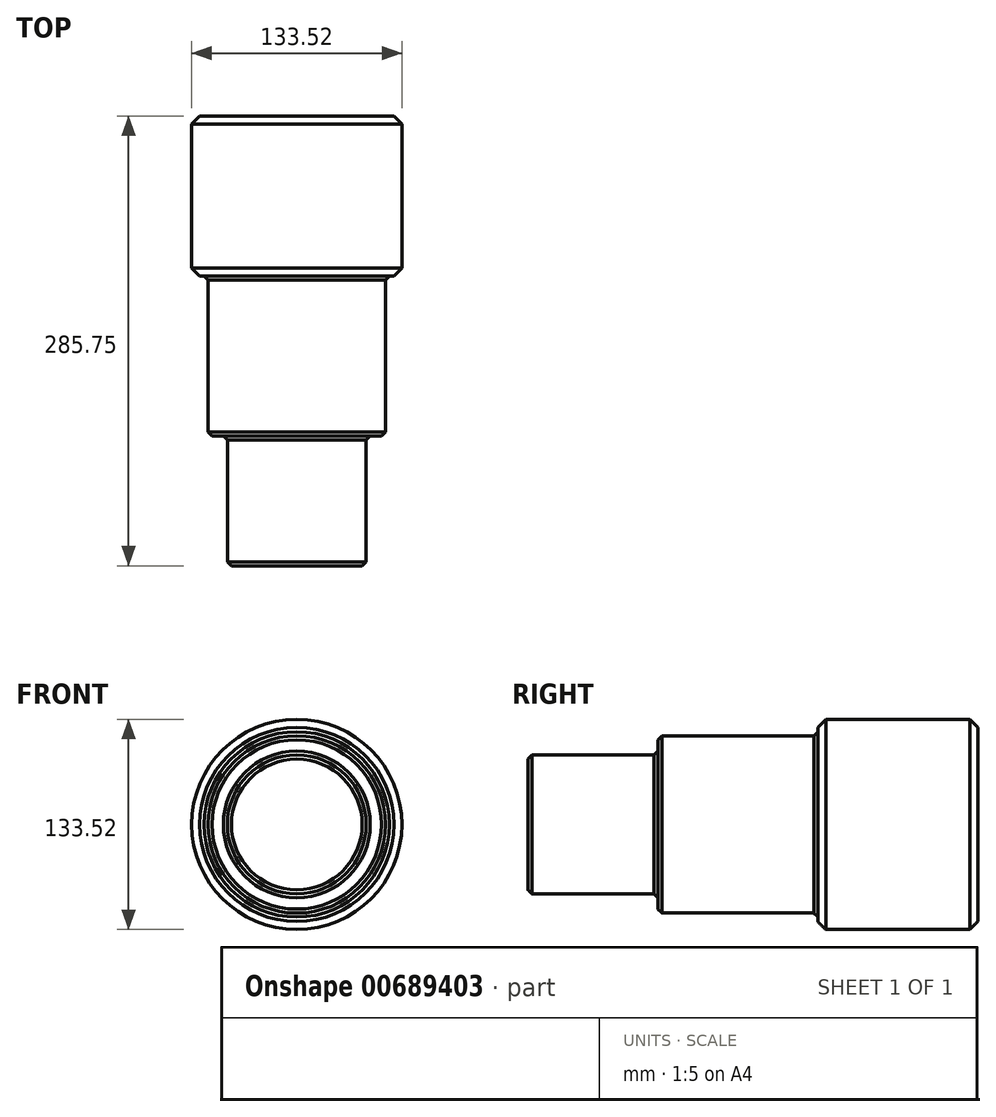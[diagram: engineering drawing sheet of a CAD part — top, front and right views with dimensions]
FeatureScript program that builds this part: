
annotation { "Feature Type Name" : "Feature", "Feature Type Description" : "" }
export const myFeature = defineFeature(function(context is Context, id is Id, definition is map)
    precondition{}
    {
        {
            var Q0;
            Q0=qCreatedBy(makeId("Front.planeOp"),FACE);
            var sketch = newSketch(context, id + "F0", { "sketchPlane" : qUnion([Q0])});
            skCircle(sketch, "E0", {"center": v(0, 0) * mm, "radius": 66.76 * mm});
            skSolve(sketch);
        }
        {
            var Q0;
            Q0 = qSketchRegion(id + "F0", true);
            extrude(context, id + "F1", {"entities" : qUnion([Q0]), "depth" : 101.6 * mm, "offsetDistance" : 25.4 * mm});
        }
        {
            var Q0;
            Q0=makeQuery(id+"F1.opExtrude","CAP_FACE",FACE,{"disambiguationData":[OSD([sQuery(id+"F0.wireOp",EDGE,"E0")])],"isStart":false});
            var sketch = newSketch(context, id + "F2", { "sketchPlane" : qUnion([Q0])});
            skCircle(sketch, "E1", {"center": v(0, 0) * mm, "radius": 56.32 * mm});
            skSolve(sketch);
        }
        {
            var Q0;
            Q0 = qSketchRegion(id + "F2", true);
            extrude(context, id + "F3", {"entities" : qUnion([Q0]), "operationType" : NewBodyOperationType.ADD, "depth" : 101.6 * mm, "offsetDistance" : 25.4 * mm});
        }
        {
            var Q0;
            Q0=makeQuery(id+"F3.opExtrude","CAP_FACE",FACE,{"disambiguationData":[OSD([sQuery(id+"F2.wireOp",EDGE,"E1")])],"isStart":false});
            var sketch = newSketch(context, id + "F4", { "sketchPlane" : qUnion([Q0])});
            skCircle(sketch, "E2", {"center": v(0, 0) * mm, "radius": 44.07 * mm});
            skSolve(sketch);
        }
        {
            var Q0;
            Q0 = qSketchRegion(id + "F4", true);
            extrude(context, id + "F5", {"entities" : qUnion([Q0]), "operationType" : NewBodyOperationType.ADD, "depth" : 82.55 * mm, "offsetDistance" : 25.4 * mm});
        }
        {
            var Q0;
            Q0=makeQuery(id+"F1.opExtrude","SWEPT_FACE",FACE,{"disambiguationData":[OSD([sQuery(id+"F0.wireOp",EDGE,"E0")])]});
            chamfer(context, id + "F6", {"entities" : qUnion([Q0]), "width" : 5.08 * mm, "tangentPropagation" : true});
        }
        {
            var Q0;
            Q0=makeQuery(id+"F3.opExtrude","SWEPT_FACE",FACE,{"disambiguationData":[OSD([sQuery(id+"F2.wireOp",EDGE,"E1")])]});
            var Q1;
            Q1=makeQuery(id+"F5.opExtrude","SWEPT_FACE",FACE,{"disambiguationData":[OSD([sQuery(id+"F4.wireOp",EDGE,"E2")])]});
            chamfer(context, id + "F7", {"entities" : qUnion([Q0, Q1]), "width" : 2.54 * mm, "tangentPropagation" : true});
        }
    });
